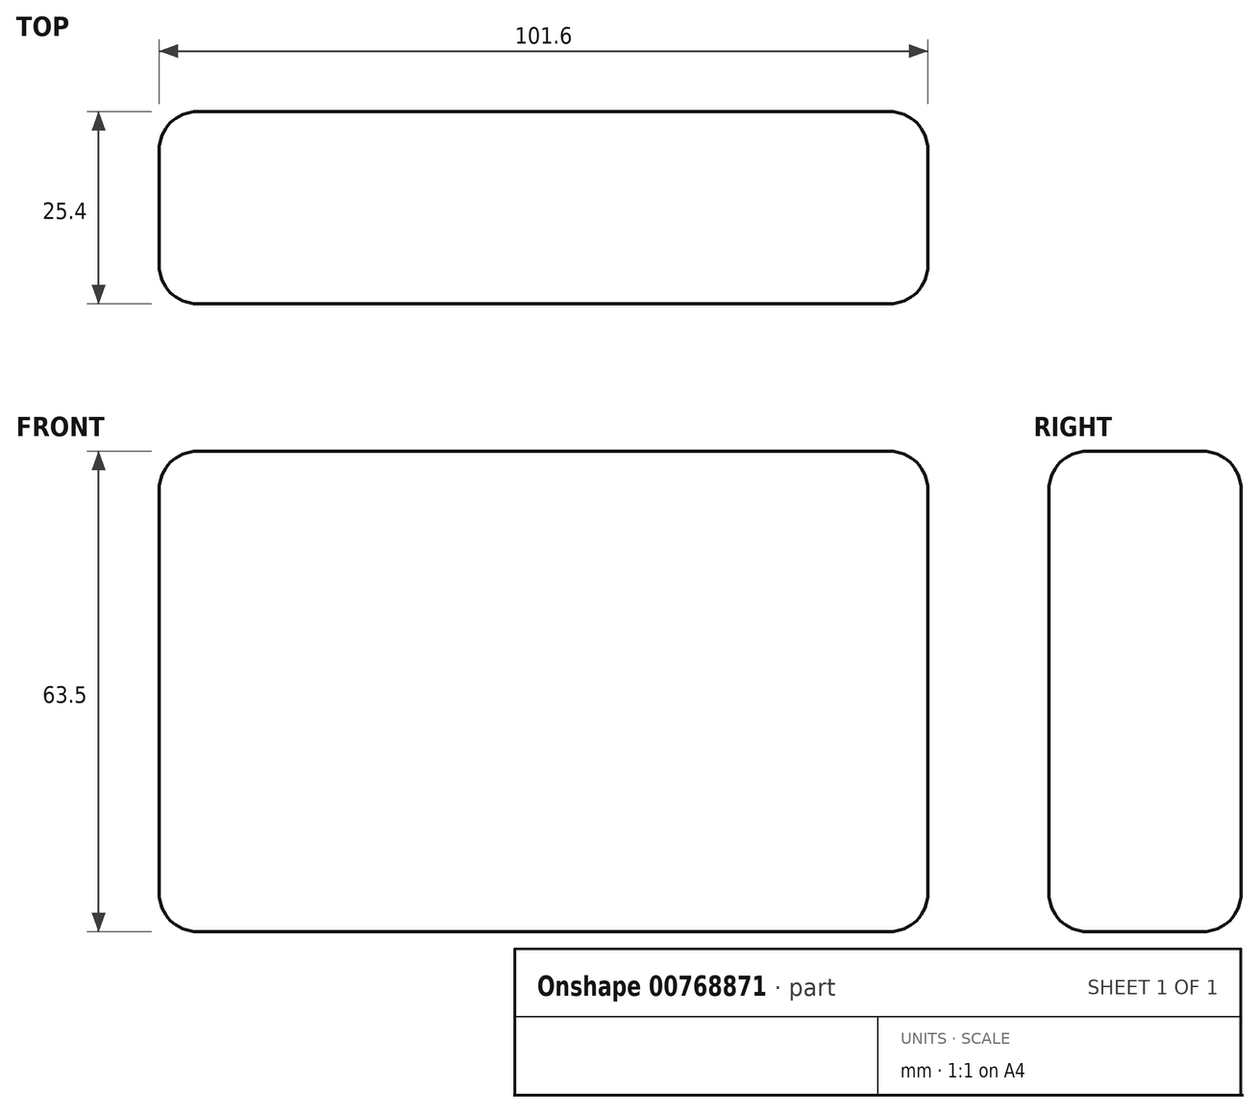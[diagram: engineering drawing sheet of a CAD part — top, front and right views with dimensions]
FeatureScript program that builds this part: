
annotation { "Feature Type Name" : "Feature", "Feature Type Description" : "" }
export const myFeature = defineFeature(function(context is Context, id is Id, definition is map)
    precondition{}
    {
        {
            var Q0;
            Q0=qCreatedBy(makeId("Front.planeOp"),FACE);
            var sketch = newSketch(context, id + "F0", { "sketchPlane" : qUnion([Q0])});
            skLineSegment(sketch, "E0.bottom", {"start": v(-50.22, 37.4) * mm, "end": v(51.38, 37.4) * mm});
            skLineSegment(sketch, "E0.top", {"start": v(-50.22, -26.1) * mm, "end": v(51.38, -26.1) * mm});
            skLineSegment(sketch, "E0.left", {"start": v(-50.22, 37.4) * mm, "end": v(-50.22, -26.1) * mm});
            skLineSegment(sketch, "E0.right", {"start": v(51.38, 37.4) * mm, "end": v(51.38, -26.1) * mm});
            skSolve(sketch);
        }
        {
            var Q0;
            Q0=makeQuery(id+"F0.imprint","IMPRINT",FACE,{"disambiguationData":[TD([[makeQuery(id+"F0.imprint","IMPRINT",EDGE,{"derivedFrom":sQuery(id+"F0.wireOp",EDGE,"E0.bottom")}),-1.0]])]});
            extrude(context, id + "F1", {"entities" : qUnion([Q0]), "depth" : 25.4 * mm, "offsetDistance" : 25.4 * mm});
        }
        {
            var Q0;
            Q0=makeQuery(id+"F1.opExtrude","CAP_EDGE",EDGE,{"disambiguationData":[OSD([sQuery(id+"F0.wireOp",EDGE,"E0.bottom")])],"isStart":false});
            var Q1;
            Q1=makeQuery(id+"F1.opExtrude","CAP_EDGE",EDGE,{"disambiguationData":[OSD([sQuery(id+"F0.wireOp",EDGE,"E0.bottom")])],"isStart":true});
            var Q2;
            Q2=makeQuery(id+"F1.opExtrude","SWEPT_EDGE",EDGE,{"disambiguationData":[OSD([sQuery(id+"F0.wireOp",EDGE,"E0.bottom"),sQuery(id+"F0.wireOp",EDGE,"E0.right")])]});
            var Q3;
            Q3=makeQuery(id+"F1.opExtrude","SWEPT_EDGE",EDGE,{"disambiguationData":[OSD([sQuery(id+"F0.wireOp",EDGE,"E0.bottom"),sQuery(id+"F0.wireOp",EDGE,"E0.left")])]});
            var Q4;
            Q4=makeQuery(id+"F1.opExtrude","CAP_EDGE",EDGE,{"disambiguationData":[OSD([sQuery(id+"F0.wireOp",EDGE,"E0.right")])],"isStart":false});
            var Q5;
            Q5=makeQuery(id+"F1.opExtrude","CAP_EDGE",EDGE,{"disambiguationData":[OSD([sQuery(id+"F0.wireOp",EDGE,"E0.right")])],"isStart":true});
            var Q6;
            Q6=makeQuery(id+"F1.opExtrude","CAP_EDGE",EDGE,{"disambiguationData":[OSD([sQuery(id+"F0.wireOp",EDGE,"E0.left")])],"isStart":false});
            var Q7;
            Q7=makeQuery(id+"F1.opExtrude","CAP_EDGE",EDGE,{"disambiguationData":[OSD([sQuery(id+"F0.wireOp",EDGE,"E0.top")])],"isStart":false});
            var Q8;
            Q8=makeQuery(id+"F1.opExtrude","CAP_EDGE",EDGE,{"disambiguationData":[OSD([sQuery(id+"F0.wireOp",EDGE,"E0.top")])],"isStart":true});
            var Q9;
            Q9=makeQuery(id+"F1.opExtrude","CAP_EDGE",EDGE,{"disambiguationData":[OSD([sQuery(id+"F0.wireOp",EDGE,"E0.left")])],"isStart":true});
            var Q10;
            Q10=makeQuery(id+"F1.opExtrude","SWEPT_EDGE",EDGE,{"disambiguationData":[OSD([sQuery(id+"F0.wireOp",EDGE,"E0.top"),sQuery(id+"F0.wireOp",EDGE,"E0.right")])]});
            var Q11;
            Q11=makeQuery(id+"F1.opExtrude","SWEPT_EDGE",EDGE,{"disambiguationData":[OSD([sQuery(id+"F0.wireOp",EDGE,"E0.top"),sQuery(id+"F0.wireOp",EDGE,"E0.left")])]});
            fillet(context, id + "F2", {"entities" : qUnion([Q0, Q1, Q2, Q3, Q4, Q5, Q6, Q7, Q8, Q9, Q10, Q11]), "radius" : 5.08 * mm, "tangentPropagation" : true, "allowEdgeOverflow" : false});
        }
    });
